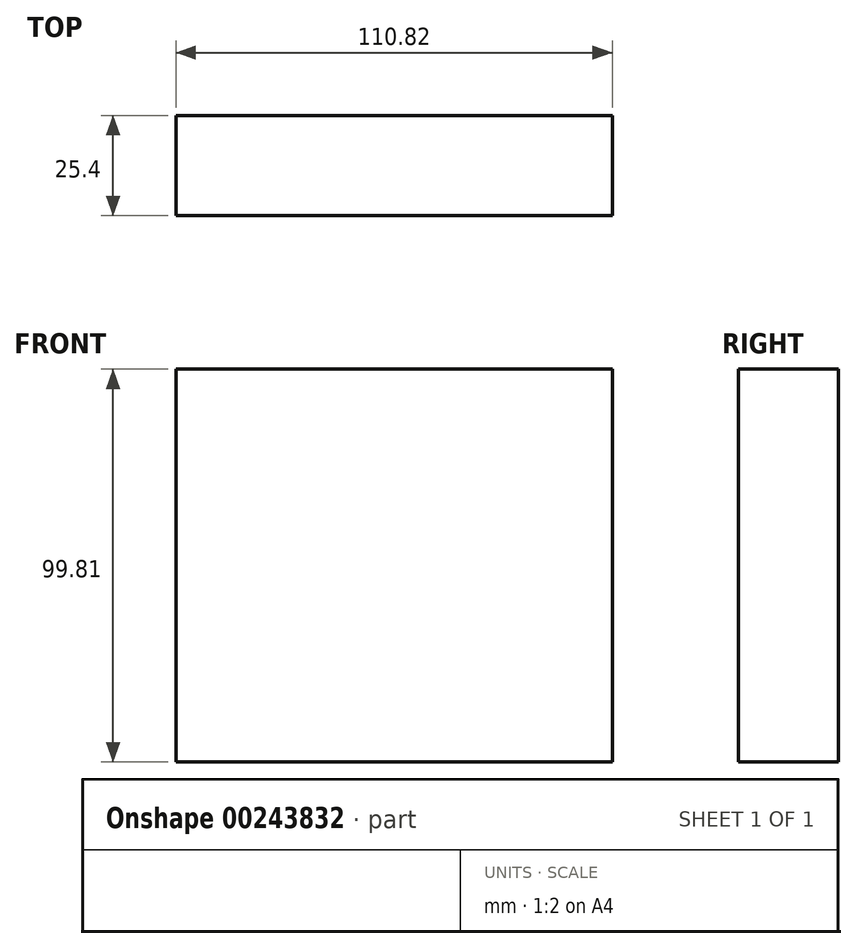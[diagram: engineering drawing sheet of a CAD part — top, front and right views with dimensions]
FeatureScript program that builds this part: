
annotation { "Feature Type Name" : "Feature", "Feature Type Description" : "" }
export const myFeature = defineFeature(function(context is Context, id is Id, definition is map)
    precondition{}
    {
        {
            var Q0;
            Q0=qCreatedBy(makeId("Front.planeOp"),FACE);
            var sketch = newSketch(context, id + "F0", { "sketchPlane" : qUnion([Q0])});
            skLineSegment(sketch, "E0.bottom", {"start": v(-6.23, 7.22) * mm, "end": v(-117.05, 7.22) * mm});
            skLineSegment(sketch, "E0.top", {"start": v(-6.23, 107.03) * mm, "end": v(-117.05, 107.03) * mm});
            skLineSegment(sketch, "E0.left", {"start": v(-6.23, 7.22) * mm, "end": v(-6.23, 107.03) * mm});
            skLineSegment(sketch, "E0.right", {"start": v(-117.05, 7.22) * mm, "end": v(-117.05, 107.03) * mm});
            skPoint(sketch, "E0.middle", {"position": v(-61.64, 57.12) * mm});
            skSolve(sketch);
        }
        {
            var Q0;
            Q0 = qSketchRegion(id + "F0", true);
            extrude(context, id + "F1", {"entities" : qUnion([Q0]), "depth" : 25.4 * mm});
        }
        {
            var Q0;
            Q0=makeQuery(id+"F1.opExtrude","CAP_FACE",FACE,{"disambiguationData":[OSD([sQuery(id+"F0.wireOp",EDGE,"E0.bottom"),sQuery(id+"F0.wireOp",EDGE,"E0.top"),sQuery(id+"F0.wireOp",EDGE,"E0.left"),sQuery(id+"F0.wireOp",EDGE,"E0.right")])],"isStart":false});
            cPlane(context, id + "F2", {"entities" : qUnion([Q0]), "cplaneType" : CPlaneType.OFFSET, "offset" : 25.4 * mm, "width" : 152.4 * mm, "height" : 152.4 * mm});
        }
        {
            var Q0;
            Q0=qCreatedBy(id+"F2.planeOp",FACE);
            cPlane(context, id + "F3", {"entities" : qUnion([Q0]), "cplaneType" : CPlaneType.OFFSET, "offset" : 25.4 * mm, "width" : 152.4 * mm, "height" : 152.4 * mm});
        }
        {
            var Q0;
            Q0=qCreatedBy(id+"F3.planeOp",FACE);
            cPlane(context, id + "F4", {"entities" : qUnion([Q0]), "cplaneType" : CPlaneType.OFFSET, "offset" : 25.4 * mm, "width" : 152.4 * mm, "height" : 152.4 * mm});
        }
        {
            var Q0;
            Q0=qCreatedBy(id+"F4.planeOp",FACE);
            cPlane(context, id + "F5", {"entities" : qUnion([Q0]), "cplaneType" : CPlaneType.OFFSET, "offset" : 25.4 * mm, "width" : 152.4 * mm, "height" : 152.4 * mm});
        }
        {
            var Q0;
            Q0=qCreatedBy(id+"F5.planeOp",FACE);
            cPlane(context, id + "F6", {"entities" : qUnion([Q0]), "cplaneType" : CPlaneType.OFFSET, "offset" : 25.4 * mm, "width" : 152.4 * mm, "height" : 152.4 * mm});
        }
        {
            var Q0;
            Q0=qCreatedBy(id+"F6.planeOp",FACE);
            cPlane(context, id + "F7", {"entities" : qUnion([Q0]), "cplaneType" : CPlaneType.OFFSET, "offset" : 25.4 * mm, "width" : 152.4 * mm, "height" : 152.4 * mm});
        }
        {
            var Q0;
            Q0=qCreatedBy(id+"F7.planeOp",FACE);
            cPlane(context, id + "F8", {"entities" : qUnion([Q0]), "cplaneType" : CPlaneType.OFFSET, "offset" : 25.4 * mm, "width" : 152.4 * mm, "height" : 152.4 * mm});
        }
        {
            var Q0;
            Q0=qCreatedBy(id+"F8.planeOp",FACE);
            cPlane(context, id + "F9", {"entities" : qUnion([Q0]), "cplaneType" : CPlaneType.OFFSET, "offset" : 25.4 * mm, "width" : 152.4 * mm, "height" : 152.4 * mm});
        }
        {
            var Q0;
            Q0=qCreatedBy(id+"F9.planeOp",FACE);
            cPlane(context, id + "F10", {"entities" : qUnion([Q0]), "cplaneType" : CPlaneType.OFFSET, "offset" : 25.4 * mm, "width" : 152.4 * mm, "height" : 152.4 * mm});
        }
        {
            var Q0;
            Q0=qCreatedBy(id+"F10.planeOp",FACE);
            cPlane(context, id + "F11", {"entities" : qUnion([Q0]), "cplaneType" : CPlaneType.OFFSET, "offset" : 25.4 * mm, "width" : 152.4 * mm, "height" : 152.4 * mm});
        }
        {
            var Q0;
            Q0=qCreatedBy(id+"F11.planeOp",FACE);
            cPlane(context, id + "F12", {"entities" : qUnion([Q0]), "cplaneType" : CPlaneType.OFFSET, "offset" : 25.4 * mm, "width" : 152.4 * mm, "height" : 152.4 * mm});
        }
        {
            var Q0;
            Q0=qCreatedBy(id+"F12.planeOp",FACE);
            cPlane(context, id + "F13", {"entities" : qUnion([Q0]), "cplaneType" : CPlaneType.OFFSET, "offset" : 25.4 * mm, "width" : 152.4 * mm, "height" : 152.4 * mm});
        }
    });
